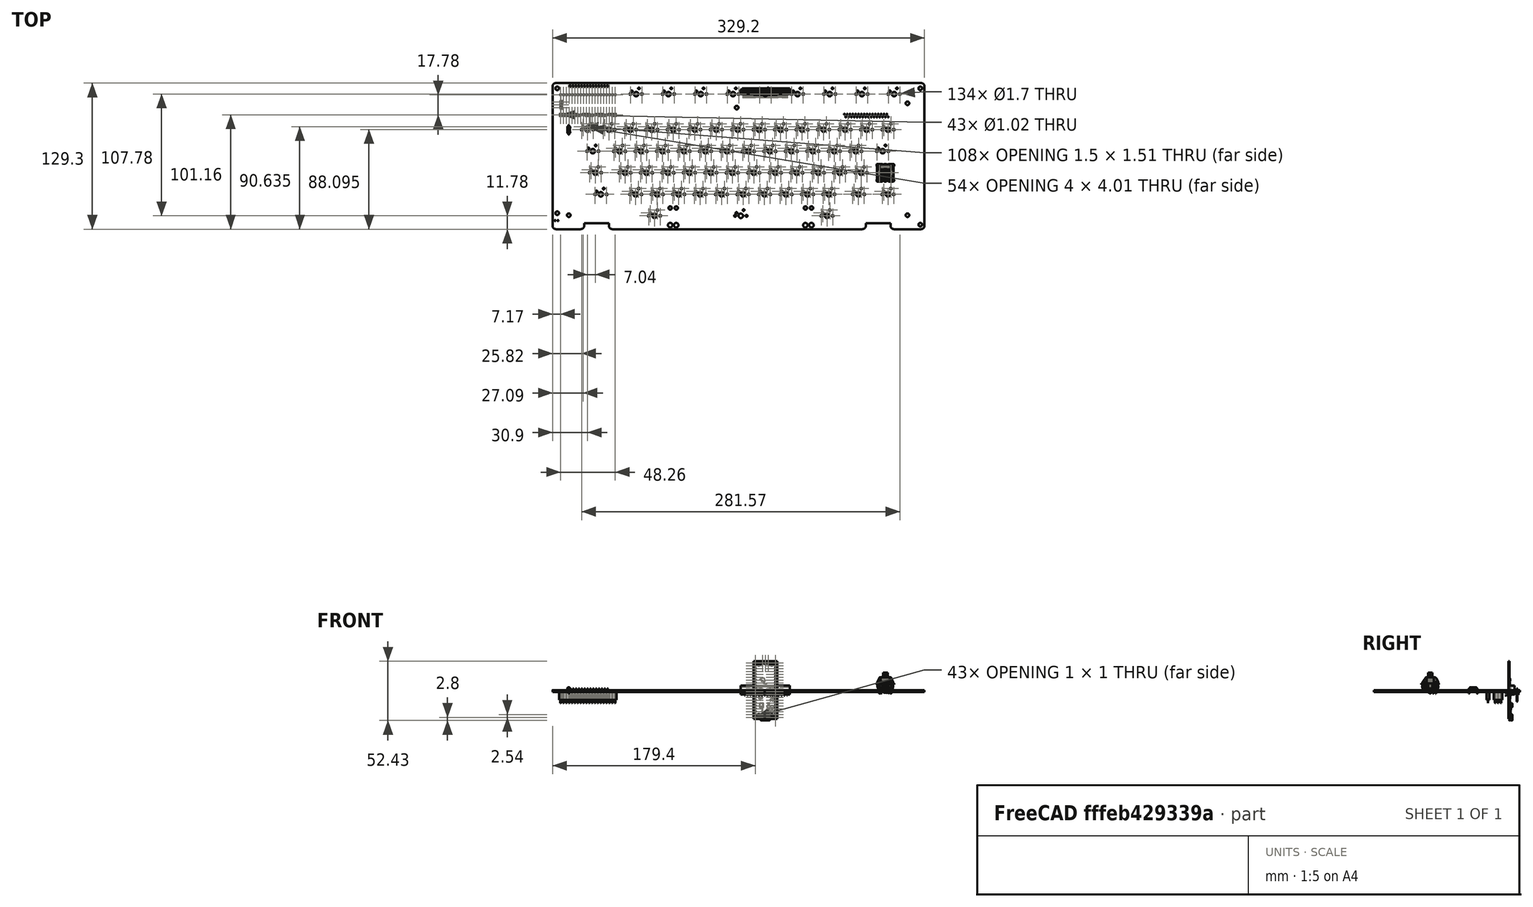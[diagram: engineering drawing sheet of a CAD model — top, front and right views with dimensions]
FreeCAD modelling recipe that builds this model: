
FCSTD DOCUMENT  (FreeCAD 0.19R)
Label: Atari130XE_MX
License: All rights reserved
LicenseURL: http://en.wikipedia.org/wiki/All_rights_reserved
objects: App::Link×126, Part::Feature×53, App::Part×7, PartDesign::CoordinateSystem×1, Sketcher::SketchObject×1
note: 55 computed .brp shape members not serialized (recipe doc carries the construction recipe); baked Part::Feature solids carry a one-line shape summary decoded from their .brp

FEATURE [PartDesign::CoordinateSystem] Local_CS_673a
  AttacherType = Attacher::AttachEngine3D
FEATURE [Part::Feature] Pcb_673a
  Placement = pos=(-211.16,32.61,0) rot=(0,0,1;0rad)
  shape: bbox 329.2 x 129.3 x 1.6 mm, 1031 faces (baked)
FEATURE [Sketcher::SketchObject] PCB_Sketch_673a
  FullyConstrained = false
  sketch-geometry (20):
    g0: LineSegment StartX=113.84 StartY=-119.55 StartZ=0 EndX=137.9 EndY=-119.55 EndZ=0
    g1: LineSegment StartX=88.94 StartY=-114.45 StartZ=0 EndX=88.94 EndY=-116.55 EndZ=0
    g2: LineSegment StartX=110.84 StartY=-114.45 StartZ=0 EndX=110.84 EndY=-116.55 EndZ=0
    g3: LineSegment StartX=88.94 StartY=-114.45 StartZ=0 EndX=110.84 EndY=-114.45 EndZ=0
    g4: LineSegment StartX=-135.4 StartY=-119.55 StartZ=0 EndX=85.94 EndY=-119.55 EndZ=0
    g5: LineSegment StartX=-138.4 StartY=-114.45 StartZ=0 EndX=-138.4 EndY=-116.55 EndZ=0
    g6: LineSegment StartX=-160.3 StartY=-114.45 StartZ=0 EndX=-138.4 EndY=-114.45 EndZ=0
    g7: LineSegment StartX=-160.3 StartY=-114.45 StartZ=0 EndX=-160.3 EndY=-116.55 EndZ=0
    g8: LineSegment StartX=-185.3 StartY=-119.55 StartZ=0 EndX=-163.3 EndY=-119.55 EndZ=0
    g9: LineSegment StartX=140.9 StartY=6.75 StartZ=0 EndX=140.9 EndY=-116.55 EndZ=0
    g10: LineSegment StartX=-185.3 StartY=9.75 StartZ=0 EndX=137.9 EndY=9.75 EndZ=0
    g11: LineSegment StartX=-188.3 StartY=6.75 StartZ=0 EndX=-188.3 EndY=-116.55 EndZ=0
    g12: ArcOfCircle CenterX=113.84 CenterY=-116.55 CenterZ=0 NormalX=0 NormalY=0 NormalZ=1 AngleXU=0 Radius=3 StartAngle=3.14159 EndAngle=4.71239
    g13: ArcOfCircle CenterX=85.94 CenterY=-116.55 CenterZ=0 NormalX=0 NormalY=0 NormalZ=1 AngleXU=0 Radius=3 StartAngle=4.71239 EndAngle=6.28319
    g14: ArcOfCircle CenterX=-135.4 CenterY=-116.55 CenterZ=0 NormalX=0 NormalY=0 NormalZ=1 AngleXU=0 Radius=3 StartAngle=3.14159 EndAngle=4.71239
    g15: ArcOfCircle CenterX=-163.3 CenterY=-116.55 CenterZ=0 NormalX=0 NormalY=0 NormalZ=1 AngleXU=0 Radius=3 StartAngle=4.71239 EndAngle=6.28319
    g16: ArcOfCircle CenterX=137.9 CenterY=-116.55 CenterZ=0 NormalX=0 NormalY=0 NormalZ=1 AngleXU=0 Radius=3 StartAngle=4.71239 EndAngle=6.28319
    g17: ArcOfCircle CenterX=137.9 CenterY=6.75 CenterZ=0 NormalX=0 NormalY=0 NormalZ=1 AngleXU=0 Radius=3 StartAngle=0 EndAngle=1.5708
    g18: ArcOfCircle CenterX=-185.3 CenterY=-116.55 CenterZ=0 NormalX=0 NormalY=0 NormalZ=1 AngleXU=0 Radius=3 StartAngle=3.14159 EndAngle=4.71239
    g19: ArcOfCircle CenterX=-185.3 CenterY=6.75 CenterZ=0 NormalX=0 NormalY=0 NormalZ=1 AngleXU=0 Radius=3 StartAngle=1.5708 EndAngle=3.14159
  constraints (20):
    c: Coincident(g18,g11)
    c: Coincident(g19,g11)
    c: Coincident(g18,g8)
    c: Coincident(g10,g19)
    c: Coincident(g8,g15)
    c: Coincident(g7,g15)
    c: Coincident(g6,g7)
    c: Coincident(g5,g14)
    c: Coincident(g5,g6)
    c: Coincident(g4,g14)
    c: Coincident(g13,g4)
    c: Coincident(g1,g13)
    c: Coincident(g3,g1)
    c: Coincident(g12,g2)
    c: Coincident(g2,g3)
    c: Coincident(g12,g0)
    c: Coincident(g16,g0)
    c: Coincident(g10,g17)
    c: Coincident(g9,g16)
    c: Coincident(g17,g9)
FEATURE [App::Part] Board_Geoms_673a
  Group = -> [Local_CS_673a,Pcb_673a,PCB_Sketch_673a]
  Origin = -> Origin
FEATURE [Part::Feature] Shape  label="SW49_SW_Cherry_MX_PCB_cp_608261B0"
  Placement = pos=(106.24,-69.62,0) rot=(0,0,1;0rad)
  shape: bbox 15.61 x 15.61 x 18.61 mm, 942 faces, 7 solids (baked)
FEATURE [App::Link] SW49_SW_Cherry_MX_PCB_cp_608261B0_ln_  label="SW49_SW_Cherry_MX_PCB_cp_608261B0[2]"
  LinkPlacement = pos=(106.24,-69.62,0) rot=(0,0,1;0rad)
  LinkedObject = -> Shape
  Placement = pos=(106.24,-69.62,0) rot=(0,0,1;0rad)
FEATURE [App::Link] SW49_SW_Cherry_MX_PCB_cp_608261B0_ln_001  label="SW19_SW_Cherry_MX_PCB_cp_6082D2A1"
  LinkPlacement = pos=(-157.4,-31.45,0) rot=(0,0,1;0rad)
  LinkedObject = -> Shape
  Placement = pos=(-157.4,-31.45,0) rot=(0,0,1;0rad)
FEATURE [App::Link] SW49_SW_Cherry_MX_PCB_cp_608261B0_ln_002  label="SW19_SW_Cherry_MX_PCB_cp_6082D2A1[2]"
  LinkPlacement = pos=(-157.4,-31.45,0) rot=(0,0,1;0rad)
  LinkedObject = -> Shape
  Placement = pos=(-157.4,-31.45,0) rot=(0,0,1;0rad)
FEATURE [App::Link] SW49_SW_Cherry_MX_PCB_cp_608261B0_ln_003  label="SW13_SW_Cherry_MX_PCB_cp_6082D337"
  LinkPlacement = pos=(-43.4,-31.45,0) rot=(0,0,1;0rad)
  LinkedObject = -> Shape
  Placement = pos=(-43.4,-31.45,0) rot=(0,0,1;0rad)
FEATURE [App::Link] SW49_SW_Cherry_MX_PCB_cp_608261B0_ln_004  label="SW13_SW_Cherry_MX_PCB_cp_6082D337[2]"
  LinkPlacement = pos=(-43.4,-31.45,0) rot=(0,0,1;0rad)
  LinkedObject = -> Shape
  Placement = pos=(-43.4,-31.45,0) rot=(0,0,1;0rad)
FEATURE [App::Link] SW49_SW_Cherry_MX_PCB_cp_608261B0_ln_005  label="SW64_SW_Cherry_MX_PCB_cp_60826667"
  LinkPlacement = pos=(-114.7,-88.72,0) rot=(0,0,1;0rad)
  LinkedObject = -> Shape
  Placement = pos=(-114.7,-88.72,0) rot=(0,0,1;0rad)
FEATURE [App::Link] SW49_SW_Cherry_MX_PCB_cp_608261B0_ln_006  label="SW64_SW_Cherry_MX_PCB_cp_60826667[2]"
  LinkPlacement = pos=(-114.7,-88.72,0) rot=(0,0,1;0rad)
  LinkedObject = -> Shape
  Placement = pos=(-114.7,-88.72,0) rot=(0,0,1;0rad)
FEATURE [App::Link] SW49_SW_Cherry_MX_PCB_cp_608261B0_ln_007  label="SW27_SW_Cherry_MX_PCB_cp_6082C6BD"
  LinkPlacement = pos=(-33.94,-50.55,0) rot=(0,0,1;0rad)
  LinkedObject = -> Shape
  Placement = pos=(-33.94,-50.55,0) rot=(0,0,1;0rad)
FEATURE [App::Link] SW49_SW_Cherry_MX_PCB_cp_608261B0_ln_008  label="SW27_SW_Cherry_MX_PCB_cp_6082C6BD[2]"
  LinkPlacement = pos=(-33.94,-50.55,0) rot=(0,0,1;0rad)
  LinkedObject = -> Shape
  Placement = pos=(-33.94,-50.55,0) rot=(0,0,1;0rad)
FEATURE [App::Link] SW49_SW_Cherry_MX_PCB_cp_608261B0_ln_009  label="SW63_SW_Cherry_MX_PCB_cp_60826633"
  LinkPlacement = pos=(-95.7,-88.72,0) rot=(0,0,1;0rad)
  LinkedObject = -> Shape
  Placement = pos=(-95.7,-88.72,0) rot=(0,0,1;0rad)
FEATURE [App::Link] SW49_SW_Cherry_MX_PCB_cp_608261B0_ln_010  label="SW63_SW_Cherry_MX_PCB_cp_60826633[2]"
  LinkPlacement = pos=(-95.7,-88.72,0) rot=(0,0,1;0rad)
  LinkedObject = -> Shape
  Placement = pos=(-95.7,-88.72,0) rot=(0,0,1;0rad)
FEATURE [App::Link] SW49_SW_Cherry_MX_PCB_cp_608261B0_ln_011  label="SW31_SW_Cherry_MX_PCB_cp_6082C672"
  LinkPlacement = pos=(-109.94,-50.55,0) rot=(0,0,1;0rad)
  LinkedObject = -> Shape
  Placement = pos=(-109.94,-50.55,0) rot=(0,0,1;0rad)
FEATURE [App::Link] SW49_SW_Cherry_MX_PCB_cp_608261B0_ln_012  label="SW31_SW_Cherry_MX_PCB_cp_6082C672[2]"
  LinkPlacement = pos=(-109.94,-50.55,0) rot=(0,0,1;0rad)
  LinkedObject = -> Shape
  Placement = pos=(-109.94,-50.55,0) rot=(0,0,1;0rad)
FEATURE [App::Link] SW49_SW_Cherry_MX_PCB_cp_608261B0_ln_013  label="SW61_SW_Cherry_MX_PCB_cp_608265FF"
  LinkPlacement = pos=(-57.7,-88.72,0) rot=(0,0,1;0rad)
  LinkedObject = -> Shape
  Placement = pos=(-57.7,-88.72,0) rot=(0,0,1;0rad)
FEATURE [App::Link] SW49_SW_Cherry_MX_PCB_cp_608261B0_ln_014  label="SW61_SW_Cherry_MX_PCB_cp_608265FF[2]"
  LinkPlacement = pos=(-57.7,-88.72,0) rot=(0,0,1;0rad)
  LinkedObject = -> Shape
  Placement = pos=(-57.7,-88.72,0) rot=(0,0,1;0rad)
FEATURE [App::Link] SW49_SW_Cherry_MX_PCB_cp_608261B0_ln_015  label="SW20_SW_Cherry_MX_PCB_cp_6082C753"
  LinkPlacement = pos=(-14.94,-50.55,0) rot=(0,0,1;0rad)
  LinkedObject = -> Shape
  Placement = pos=(-14.94,-50.55,0) rot=(0,0,1;0rad)
FEATURE [App::Link] SW49_SW_Cherry_MX_PCB_cp_608261B0_ln_016  label="SW20_SW_Cherry_MX_PCB_cp_6082C753[2]"
  LinkPlacement = pos=(-14.94,-50.55,0) rot=(0,0,1;0rad)
  LinkedObject = -> Shape
  Placement = pos=(-14.94,-50.55,0) rot=(0,0,1;0rad)
FEATURE [App::Link] SW49_SW_Cherry_MX_PCB_cp_608261B0_ln_017  label="SW28_SW_Cherry_MX_PCB_cp_6082C708"
  LinkPlacement = pos=(-52.94,-50.55,0) rot=(0,0,1;0rad)
  LinkedObject = -> Shape
  Placement = pos=(-52.94,-50.55,0) rot=(0,0,1;0rad)
FEATURE [App::Link] SW49_SW_Cherry_MX_PCB_cp_608261B0_ln_018  label="SW28_SW_Cherry_MX_PCB_cp_6082C708[2]"
  LinkPlacement = pos=(-52.94,-50.55,0) rot=(0,0,1;0rad)
  LinkedObject = -> Shape
  Placement = pos=(-52.94,-50.55,0) rot=(0,0,1;0rad)
FEATURE [App::Link] SW49_SW_Cherry_MX_PCB_cp_608261B0_ln_019  label="SW40_SW_Cherry_MX_PCB_cp_61426050"
  LinkPlacement = pos=(84.84,-69.62,0) rot=(0,0,1;0rad)
  LinkedObject = -> Shape
  Placement = pos=(84.84,-69.62,0) rot=(0,0,1;0rad)
FEATURE [App::Link] SW49_SW_Cherry_MX_PCB_cp_608261B0_ln_020  label="SW40_SW_Cherry_MX_PCB_cp_61426050[2]"
  LinkPlacement = pos=(84.84,-69.62,0) rot=(0,0,1;0rad)
  LinkedObject = -> Shape
  Placement = pos=(84.84,-69.62,0) rot=(0,0,1;0rad)
FEATURE [App::Link] SW49_SW_Cherry_MX_PCB_cp_608261B0_ln_021  label="SW56_SW_Cherry_MX_PCB_cp_6082654A"
  LinkPlacement = pos=(56.3,-88.72,0) rot=(0,0,1;0rad)
  LinkedObject = -> Shape
  Placement = pos=(56.3,-88.72,0) rot=(0,0,1;0rad)
FEATURE [App::Link] SW49_SW_Cherry_MX_PCB_cp_608261B0_ln_022  label="SW56_SW_Cherry_MX_PCB_cp_6082654A[2]"
  LinkPlacement = pos=(56.3,-88.72,0) rot=(0,0,1;0rad)
  LinkedObject = -> Shape
  Placement = pos=(56.3,-88.72,0) rot=(0,0,1;0rad)
FEATURE [App::Link] SW49_SW_Cherry_MX_PCB_cp_608261B0_ln_023  label="SW38_SW_Cherry_MX_PCB_cp_60826530"
  LinkPlacement = pos=(46.84,-69.62,0) rot=(0,0,1;0rad)
  LinkedObject = -> Shape
  Placement = pos=(46.84,-69.62,0) rot=(0,0,1;0rad)
FEATURE [App::Link] SW49_SW_Cherry_MX_PCB_cp_608261B0_ln_024  label="SW38_SW_Cherry_MX_PCB_cp_60826530[2]"
  LinkPlacement = pos=(46.84,-69.62,0) rot=(0,0,1;0rad)
  LinkedObject = -> Shape
  Placement = pos=(46.84,-69.62,0) rot=(0,0,1;0rad)
FEATURE [App::Link] SW49_SW_Cherry_MX_PCB_cp_608261B0_ln_025  label="SW47_SW_Cherry_MX_PCB_cp_608264FC"
  LinkPlacement = pos=(-105.16,-69.62,0) rot=(0,0,1;0rad)
  LinkedObject = -> Shape
  Placement = pos=(-105.16,-69.62,0) rot=(0,0,1;0rad)
FEATURE [App::Link] SW49_SW_Cherry_MX_PCB_cp_608261B0_ln_026  label="SW47_SW_Cherry_MX_PCB_cp_608264FC[2]"
  LinkPlacement = pos=(-105.16,-69.62,0) rot=(0,0,1;0rad)
  LinkedObject = -> Shape
  Placement = pos=(-105.16,-69.62,0) rot=(0,0,1;0rad)
FEATURE [App::Link] SW49_SW_Cherry_MX_PCB_cp_608261B0_ln_027  label="SW29_SW_Cherry_MX_PCB_cp_6082CC99"
  LinkPlacement = pos=(-71.94,-50.55,0) rot=(0,0,1;0rad)
  LinkedObject = -> Shape
  Placement = pos=(-71.94,-50.55,0) rot=(0,0,1;0rad)
FEATURE [App::Link] SW49_SW_Cherry_MX_PCB_cp_608261B0_ln_028  label="SW29_SW_Cherry_MX_PCB_cp_6082CC99[2]"
  LinkPlacement = pos=(-71.94,-50.55,0) rot=(0,0,1;0rad)
  LinkedObject = -> Shape
  Placement = pos=(-71.94,-50.55,0) rot=(0,0,1;0rad)
FEATURE [App::Link] SW49_SW_Cherry_MX_PCB_cp_608261B0_ln_029  label="SW32_SW_Cherry_MX_PCB_cp_6082C87F"
  LinkPlacement = pos=(-128.94,-50.55,0) rot=(0,0,1;0rad)
  LinkedObject = -> Shape
  Placement = pos=(-128.94,-50.55,0) rot=(0,0,1;0rad)
FEATURE [App::Link] SW49_SW_Cherry_MX_PCB_cp_608261B0_ln_030  label="SW32_SW_Cherry_MX_PCB_cp_6082C87F[2]"
  LinkPlacement = pos=(-128.94,-50.55,0) rot=(0,0,1;0rad)
  LinkedObject = -> Shape
  Placement = pos=(-128.94,-50.55,0) rot=(0,0,1;0rad)
FEATURE [App::Link] SW49_SW_Cherry_MX_PCB_cp_608261B0_ln_031  label="SW39_SW_Cherry_MX_PCB_cp_6082645C"
  LinkPlacement = pos=(65.84,-69.62,0) rot=(0,0,1;0rad)
  LinkedObject = -> Shape
  Placement = pos=(65.84,-69.62,0) rot=(0,0,1;0rad)
FEATURE [App::Link] SW49_SW_Cherry_MX_PCB_cp_608261B0_ln_032  label="SW39_SW_Cherry_MX_PCB_cp_6082645C[2]"
  LinkPlacement = pos=(65.84,-69.62,0) rot=(0,0,1;0rad)
  LinkedObject = -> Shape
  Placement = pos=(65.84,-69.62,0) rot=(0,0,1;0rad)
FEATURE [App::Link] SW49_SW_Cherry_MX_PCB_cp_608261B0_ln_033  label="SW55_SW_Cherry_MX_PCB_cp_60826442"
  LinkPlacement = pos=(37.3,-88.72,0) rot=(0,0,1;0rad)
  LinkedObject = -> Shape
  Placement = pos=(37.3,-88.72,0) rot=(0,0,1;0rad)
FEATURE [App::Link] SW49_SW_Cherry_MX_PCB_cp_608261B0_ln_034  label="SW55_SW_Cherry_MX_PCB_cp_60826442[2]"
  LinkPlacement = pos=(37.3,-88.72,0) rot=(0,0,1;0rad)
  LinkedObject = -> Shape
  Placement = pos=(37.3,-88.72,0) rot=(0,0,1;0rad)
FEATURE [App::Link] SW49_SW_Cherry_MX_PCB_cp_608261B0_ln_035  label="SW23_SW_Cherry_MX_PCB_cp_6082C834"
  LinkPlacement = pos=(42.06,-50.55,0) rot=(0,0,1;0rad)
  LinkedObject = -> Shape
  Placement = pos=(42.06,-50.55,0) rot=(0,0,1;0rad)
FEATURE [App::Link] SW49_SW_Cherry_MX_PCB_cp_608261B0_ln_036  label="SW23_SW_Cherry_MX_PCB_cp_6082C834[2]"
  LinkPlacement = pos=(42.06,-50.55,0) rot=(0,0,1;0rad)
  LinkedObject = -> Shape
  Placement = pos=(42.06,-50.55,0) rot=(0,0,1;0rad)
FEATURE [App::Link] SW49_SW_Cherry_MX_PCB_cp_608261B0_ln_037  label="SW22_SW_Cherry_MX_PCB_cp_6082CDC5"
  LinkPlacement = pos=(23.06,-50.55,0) rot=(0,0,1;0rad)
  LinkedObject = -> Shape
  Placement = pos=(23.06,-50.55,0) rot=(0,0,1;0rad)
FEATURE [App::Link] SW49_SW_Cherry_MX_PCB_cp_608261B0_ln_038  label="SW22_SW_Cherry_MX_PCB_cp_6082CDC5[2]"
  LinkPlacement = pos=(23.06,-50.55,0) rot=(0,0,1;0rad)
  LinkedObject = -> Shape
  Placement = pos=(23.06,-50.55,0) rot=(0,0,1;0rad)
FEATURE [App::Link] SW49_SW_Cherry_MX_PCB_cp_608261B0_ln_039  label="SW51_SW_Cherry_MX_PCB_cp_608263DA"
  LinkPlacement = pos=(-19.7,-88.72,0) rot=(0,0,1;0rad)
  LinkedObject = -> Shape
  Placement = pos=(-19.7,-88.72,0) rot=(0,0,1;0rad)
FEATURE [App::Link] SW49_SW_Cherry_MX_PCB_cp_608261B0_ln_040  label="SW51_SW_Cherry_MX_PCB_cp_608263DA[2]"
  LinkPlacement = pos=(-19.7,-88.72,0) rot=(0,0,1;0rad)
  LinkedObject = -> Shape
  Placement = pos=(-19.7,-88.72,0) rot=(0,0,1;0rad)
FEATURE [App::Link] SW49_SW_Cherry_MX_PCB_cp_608261B0_ln_041  label="SW53_SW_Cherry_MX_PCB_cp_608263C0"
  LinkPlacement = pos=(-0.7,-88.72,0) rot=(0,0,1;0rad)
  LinkedObject = -> Shape
  Placement = pos=(-0.7,-88.72,0) rot=(0,0,1;0rad)
FEATURE [App::Link] SW49_SW_Cherry_MX_PCB_cp_608261B0_ln_042  label="SW53_SW_Cherry_MX_PCB_cp_608263C0[2]"
  LinkPlacement = pos=(-0.7,-88.72,0) rot=(0,0,1;0rad)
  LinkedObject = -> Shape
  Placement = pos=(-0.7,-88.72,0) rot=(0,0,1;0rad)
FEATURE [App::Link] SW49_SW_Cherry_MX_PCB_cp_608261B0_ln_043  label="SW5_SW_Cherry_MX_PCB_cp_6082D5DA"
  LinkPlacement = pos=(51.6,-31.45,0) rot=(0,0,1;0rad)
  LinkedObject = -> Shape
  Placement = pos=(51.6,-31.45,0) rot=(0,0,1;0rad)
FEATURE [App::Link] SW49_SW_Cherry_MX_PCB_cp_608261B0_ln_044  label="SW5_SW_Cherry_MX_PCB_cp_6082D5DA[2]"
  LinkPlacement = pos=(51.6,-31.45,0) rot=(0,0,1;0rad)
  LinkedObject = -> Shape
  Placement = pos=(51.6,-31.45,0) rot=(0,0,1;0rad)
FEATURE [App::Link] SW49_SW_Cherry_MX_PCB_cp_608261B0_ln_045  label="SW37_SW_Cherry_MX_PCB_cp_6082636E"
  LinkPlacement = pos=(27.84,-69.62,0) rot=(0,0,1;0rad)
  LinkedObject = -> Shape
  Placement = pos=(27.84,-69.62,0) rot=(0,0,1;0rad)
FEATURE [App::Link] SW49_SW_Cherry_MX_PCB_cp_608261B0_ln_046  label="SW37_SW_Cherry_MX_PCB_cp_6082636E[2]"
  LinkPlacement = pos=(27.84,-69.62,0) rot=(0,0,1;0rad)
  LinkedObject = -> Shape
  Placement = pos=(27.84,-69.62,0) rot=(0,0,1;0rad)
FEATURE [App::Link] SW49_SW_Cherry_MX_PCB_cp_608261B0_ln_047  label="SW36_SW_Cherry_MX_PCB_cp_60826354"
  LinkPlacement = pos=(8.84,-69.62,0) rot=(0,0,1;0rad)
  LinkedObject = -> Shape
  Placement = pos=(8.84,-69.62,0) rot=(0,0,1;0rad)
FEATURE [App::Link] SW49_SW_Cherry_MX_PCB_cp_608261B0_ln_048  label="SW36_SW_Cherry_MX_PCB_cp_60826354[2]"
  LinkPlacement = pos=(8.84,-69.62,0) rot=(0,0,1;0rad)
  LinkedObject = -> Shape
  Placement = pos=(8.84,-69.62,0) rot=(0,0,1;0rad)
FEATURE [App::Link] SW49_SW_Cherry_MX_PCB_cp_608261B0_ln_049  label="SW35_SW_Cherry_MX_PCB_cp_6082633A"
  LinkPlacement = pos=(-10.16,-69.62,0) rot=(0,0,1;0rad)
  LinkedObject = -> Shape
  Placement = pos=(-10.16,-69.62,0) rot=(0,0,1;0rad)
FEATURE [App::Link] SW49_SW_Cherry_MX_PCB_cp_608261B0_ln_050  label="SW35_SW_Cherry_MX_PCB_cp_6082633A[2]"
  LinkPlacement = pos=(-10.16,-69.62,0) rot=(0,0,1;0rad)
  LinkedObject = -> Shape
  Placement = pos=(-10.16,-69.62,0) rot=(0,0,1;0rad)
FEATURE [App::Link] SW49_SW_Cherry_MX_PCB_cp_608261B0_ln_051  label="SW57_SW_Cherry_MX_PCB_cp_60826320"
  LinkPlacement = pos=(108.6,-88.72,0) rot=(0,0,1;0rad)
  LinkedObject = -> Shape
  Placement = pos=(108.6,-88.72,0) rot=(0,0,1;0rad)
FEATURE [App::Link] SW49_SW_Cherry_MX_PCB_cp_608261B0_ln_052  label="SW57_SW_Cherry_MX_PCB_cp_60826320[2]"
  LinkPlacement = pos=(108.6,-88.72,0) rot=(0,0,1;0rad)
  LinkedObject = -> Shape
  Placement = pos=(108.6,-88.72,0) rot=(0,0,1;0rad)
FEATURE [App::Link] SW49_SW_Cherry_MX_PCB_cp_608261B0_ln_053  label="SW21_SW_Cherry_MX_PCB_cp_6082C915"
  LinkPlacement = pos=(4.06,-50.55,0) rot=(0,0,1;0rad)
  LinkedObject = -> Shape
  Placement = pos=(4.06,-50.55,0) rot=(0,0,1;0rad)
FEATURE [App::Link] SW49_SW_Cherry_MX_PCB_cp_608261B0_ln_054  label="SW21_SW_Cherry_MX_PCB_cp_6082C915[2]"
  LinkPlacement = pos=(4.06,-50.55,0) rot=(0,0,1;0rad)
  LinkedObject = -> Shape
  Placement = pos=(4.06,-50.55,0) rot=(0,0,1;0rad)
FEATURE [App::Link] SW49_SW_Cherry_MX_PCB_cp_608261B0_ln_055  label="SW43_SW_Cherry_MX_PCB_cp_608262D2"
  LinkPlacement = pos=(-29.16,-69.62,0) rot=(0,0,1;0rad)
  LinkedObject = -> Shape
  Placement = pos=(-29.16,-69.62,0) rot=(0,0,1;0rad)
FEATURE [App::Link] SW49_SW_Cherry_MX_PCB_cp_608261B0_ln_056  label="SW43_SW_Cherry_MX_PCB_cp_608262D2[2]"
  LinkPlacement = pos=(-29.16,-69.62,0) rot=(0,0,1;0rad)
  LinkedObject = -> Shape
  Placement = pos=(-29.16,-69.62,0) rot=(0,0,1;0rad)
FEATURE [App::Link] SW49_SW_Cherry_MX_PCB_cp_608261B0_ln_057  label="SW6_SW_Cherry_MX_PCB_cp_6082D4F9"
  LinkPlacement = pos=(70.6,-31.45,0) rot=(0,0,1;0rad)
  LinkedObject = -> Shape
  Placement = pos=(70.6,-31.45,0) rot=(0,0,1;0rad)
FEATURE [App::Link] SW49_SW_Cherry_MX_PCB_cp_608261B0_ln_058  label="SW6_SW_Cherry_MX_PCB_cp_6082D4F9[2]"
  LinkPlacement = pos=(70.6,-31.45,0) rot=(0,0,1;0rad)
  LinkedObject = -> Shape
  Placement = pos=(70.6,-31.45,0) rot=(0,0,1;0rad)
FEATURE [App::Link] SW49_SW_Cherry_MX_PCB_cp_608261B0_ln_059  label="SW44_SW_Cherry_MX_PCB_cp_6082629E"
  LinkPlacement = pos=(-48.16,-69.62,0) rot=(0,0,1;0rad)
  LinkedObject = -> Shape
  Placement = pos=(-48.16,-69.62,0) rot=(0,0,1;0rad)
FEATURE [App::Link] SW49_SW_Cherry_MX_PCB_cp_608261B0_ln_060  label="SW44_SW_Cherry_MX_PCB_cp_6082629E[2]"
  LinkPlacement = pos=(-48.16,-69.62,0) rot=(0,0,1;0rad)
  LinkedObject = -> Shape
  Placement = pos=(-48.16,-69.62,0) rot=(0,0,1;0rad)
FEATURE [App::Link] SW49_SW_Cherry_MX_PCB_cp_608261B0_ln_061  label="SW25_SW_Cherry_MX_PCB_cp_6082C9AB"
  LinkPlacement = pos=(80.06,-50.55,0) rot=(0,0,1;0rad)
  LinkedObject = -> Shape
  Placement = pos=(80.06,-50.55,0) rot=(0,0,1;0rad)
FEATURE [App::Link] SW49_SW_Cherry_MX_PCB_cp_608261B0_ln_062  label="SW25_SW_Cherry_MX_PCB_cp_6082C9AB[2]"
  LinkPlacement = pos=(80.06,-50.55,0) rot=(0,0,1;0rad)
  LinkedObject = -> Shape
  Placement = pos=(80.06,-50.55,0) rot=(0,0,1;0rad)
FEATURE [App::Link] SW49_SW_Cherry_MX_PCB_cp_608261B0_ln_063  label="SW30_SW_Cherry_MX_PCB_cp_6082CCE4"
  LinkPlacement = pos=(-90.94,-50.55,0) rot=(0,0,1;0rad)
  LinkedObject = -> Shape
  Placement = pos=(-90.94,-50.55,0) rot=(0,0,1;0rad)
FEATURE [App::Link] SW49_SW_Cherry_MX_PCB_cp_608261B0_ln_064  label="SW30_SW_Cherry_MX_PCB_cp_6082CCE4[2]"
  LinkPlacement = pos=(-90.94,-50.55,0) rot=(0,0,1;0rad)
  LinkedObject = -> Shape
  Placement = pos=(-90.94,-50.55,0) rot=(0,0,1;0rad)
FEATURE [App::Link] SW49_SW_Cherry_MX_PCB_cp_608261B0_ln_065  label="SW7_SW_Cherry_MX_PCB_cp_6082D463"
  LinkPlacement = pos=(89.6,-31.45,0) rot=(0,0,1;0rad)
  LinkedObject = -> Shape
  Placement = pos=(89.6,-31.45,0) rot=(0,0,1;0rad)
FEATURE [App::Link] SW49_SW_Cherry_MX_PCB_cp_608261B0_ln_066  label="SW7_SW_Cherry_MX_PCB_cp_6082D463[2]"
  LinkPlacement = pos=(89.6,-31.45,0) rot=(0,0,1;0rad)
  LinkedObject = -> Shape
  Placement = pos=(89.6,-31.45,0) rot=(0,0,1;0rad)
FEATURE [App::Link] SW49_SW_Cherry_MX_PCB_cp_608261B0_ln_067  label="SW24_SW_Cherry_MX_PCB_cp_6082CA41"
  LinkPlacement = pos=(61.06,-50.55,0) rot=(0,0,1;0rad)
  LinkedObject = -> Shape
  Placement = pos=(61.06,-50.55,0) rot=(0,0,1;0rad)
FEATURE [App::Link] SW49_SW_Cherry_MX_PCB_cp_608261B0_ln_068  label="SW24_SW_Cherry_MX_PCB_cp_6082CA41[2]"
  LinkPlacement = pos=(61.06,-50.55,0) rot=(0,0,1;0rad)
  LinkedObject = -> Shape
  Placement = pos=(61.06,-50.55,0) rot=(0,0,1;0rad)
FEATURE [App::Link] SW49_SW_Cherry_MX_PCB_cp_608261B0_ln_069  label="SW46_SW_Cherry_MX_PCB_cp_6100000000.0"
  LinkPlacement = pos=(-86.16,-69.62,0) rot=(0,0,1;0rad)
  LinkedObject = -> Shape
  Placement = pos=(-86.16,-69.62,0) rot=(0,0,1;0rad)
FEATURE [App::Link] SW49_SW_Cherry_MX_PCB_cp_608261B0_ln_070  label="SW46_SW_Cherry_MX_PCB_cp_6100000000.0[2]"
  LinkPlacement = pos=(-86.16,-69.62,0) rot=(0,0,1;0rad)
  LinkedObject = -> Shape
  Placement = pos=(-86.16,-69.62,0) rot=(0,0,1;0rad)
FEATURE [App::Link] SW49_SW_Cherry_MX_PCB_cp_608261B0_ln_071  label="SW54_SW_Cherry_MX_PCB_cp_60826196"
  LinkPlacement = pos=(18.3,-88.72,0) rot=(0,0,1;0rad)
  LinkedObject = -> Shape
  Placement = pos=(18.3,-88.72,0) rot=(0,0,1;0rad)
FEATURE [App::Link] SW49_SW_Cherry_MX_PCB_cp_608261B0_ln_072  label="SW54_SW_Cherry_MX_PCB_cp_60826196[2]"
  LinkPlacement = pos=(18.3,-88.72,0) rot=(0,0,1;0rad)
  LinkedObject = -> Shape
  Placement = pos=(18.3,-88.72,0) rot=(0,0,1;0rad)
FEATURE [App::Link] SW49_SW_Cherry_MX_PCB_cp_608261B0_ln_073  label="SW62_SW_Cherry_MX_PCB_cp_6082617C"
  LinkPlacement = pos=(-76.7,-88.72,0) rot=(0,0,1;0rad)
  LinkedObject = -> Shape
  Placement = pos=(-76.7,-88.72,0) rot=(0,0,1;0rad)
FEATURE [App::Link] SW49_SW_Cherry_MX_PCB_cp_608261B0_ln_074  label="SW62_SW_Cherry_MX_PCB_cp_6082617C[2]"
  LinkPlacement = pos=(-76.7,-88.72,0) rot=(0,0,1;0rad)
  LinkedObject = -> Shape
  Placement = pos=(-76.7,-88.72,0) rot=(0,0,1;0rad)
FEATURE [App::Link] SW49_SW_Cherry_MX_PCB_cp_608261B0_ln_075  label="SW8_SW_Cherry_MX_PCB_cp_6082D625"
  LinkPlacement = pos=(108.6,-31.45,0) rot=(0,0,1;0rad)
  LinkedObject = -> Shape
  Placement = pos=(108.6,-31.45,0) rot=(0,0,1;0rad)
FEATURE [App::Link] SW49_SW_Cherry_MX_PCB_cp_608261B0_ln_076  label="SW8_SW_Cherry_MX_PCB_cp_6082D625[2]"
  LinkPlacement = pos=(108.6,-31.45,0) rot=(0,0,1;0rad)
  LinkedObject = -> Shape
  Placement = pos=(108.6,-31.45,0) rot=(0,0,1;0rad)
FEATURE [App::Link] SW49_SW_Cherry_MX_PCB_cp_608261B0_ln_077  label="SW60_SW_Cherry_MX_PCB_cp_60826148"
  LinkPlacement = pos=(-38.7,-88.72,0) rot=(0,0,1;0rad)
  LinkedObject = -> Shape
  Placement = pos=(-38.7,-88.72,0) rot=(0,0,1;0rad)
FEATURE [App::Link] SW49_SW_Cherry_MX_PCB_cp_608261B0_ln_078  label="SW60_SW_Cherry_MX_PCB_cp_60826148[2]"
  LinkPlacement = pos=(-38.7,-88.72,0) rot=(0,0,1;0rad)
  LinkedObject = -> Shape
  Placement = pos=(-38.7,-88.72,0) rot=(0,0,1;0rad)
FEATURE [App::Link] SW49_SW_Cherry_MX_PCB_cp_608261B0_ln_079  label="SW48_SW_Cherry_MX_PCB_cp_6082612E"
  LinkPlacement = pos=(-124.16,-69.62,0) rot=(0,0,1;0rad)
  LinkedObject = -> Shape
  Placement = pos=(-124.16,-69.62,0) rot=(0,0,1;0rad)
FEATURE [App::Link] SW49_SW_Cherry_MX_PCB_cp_608261B0_ln_080  label="SW48_SW_Cherry_MX_PCB_cp_6082612E[2]"
  LinkPlacement = pos=(-124.16,-69.62,0) rot=(0,0,1;0rad)
  LinkedObject = -> Shape
  Placement = pos=(-124.16,-69.62,0) rot=(0,0,1;0rad)
FEATURE [App::Link] SW49_SW_Cherry_MX_PCB_cp_608261B0_ln_081  label="SW3_SW_Cherry_MX_PCB_cp_6082D382"
  LinkPlacement = pos=(13.6,-31.45,0) rot=(0,0,1;0rad)
  LinkedObject = -> Shape
  Placement = pos=(13.6,-31.45,0) rot=(0,0,1;0rad)
FEATURE [App::Link] SW49_SW_Cherry_MX_PCB_cp_608261B0_ln_082  label="SW3_SW_Cherry_MX_PCB_cp_6082D382[2]"
  LinkPlacement = pos=(13.6,-31.45,0) rot=(0,0,1;0rad)
  LinkedObject = -> Shape
  Placement = pos=(13.6,-31.45,0) rot=(0,0,1;0rad)
FEATURE [App::Link] SW49_SW_Cherry_MX_PCB_cp_608261B0_ln_083  label="SW2_SW_Cherry_MX_PCB_cp_6082D2EC"
  LinkPlacement = pos=(-5.4,-31.45,0) rot=(0,0,1;0rad)
  LinkedObject = -> Shape
  Placement = pos=(-5.4,-31.45,0) rot=(0,0,1;0rad)
FEATURE [App::Link] SW49_SW_Cherry_MX_PCB_cp_608261B0_ln_084  label="SW2_SW_Cherry_MX_PCB_cp_6082D2EC[2]"
  LinkPlacement = pos=(-5.4,-31.45,0) rot=(0,0,1;0rad)
  LinkedObject = -> Shape
  Placement = pos=(-5.4,-31.45,0) rot=(0,0,1;0rad)
FEATURE [App::Link] SW49_SW_Cherry_MX_PCB_cp_608261B0_ln_085  label="SW1_SW_Cherry_MX_PCB_cp_6082D6BB"
  LinkPlacement = pos=(-24.4,-31.45,0) rot=(0,0,1;0rad)
  LinkedObject = -> Shape
  Placement = pos=(-24.4,-31.45,0) rot=(0,0,1;0rad)
FEATURE [App::Link] SW49_SW_Cherry_MX_PCB_cp_608261B0_ln_086  label="SW1_SW_Cherry_MX_PCB_cp_6082D6BB[2]"
  LinkPlacement = pos=(-24.4,-31.45,0) rot=(0,0,1;0rad)
  LinkedObject = -> Shape
  Placement = pos=(-24.4,-31.45,0) rot=(0,0,1;0rad)
FEATURE [App::Link] SW49_SW_Cherry_MX_PCB_cp_608261B0_ln_087  label="SW14_SW_Cherry_MX_PCB_cp_6082D418"
  LinkPlacement = pos=(-62.4,-31.45,0) rot=(0,0,1;0rad)
  LinkedObject = -> Shape
  Placement = pos=(-62.4,-31.45,0) rot=(0,0,1;0rad)
FEATURE [App::Link] SW49_SW_Cherry_MX_PCB_cp_608261B0_ln_088  label="SW14_SW_Cherry_MX_PCB_cp_6082D418[2]"
  LinkPlacement = pos=(-62.4,-31.45,0) rot=(0,0,1;0rad)
  LinkedObject = -> Shape
  Placement = pos=(-62.4,-31.45,0) rot=(0,0,1;0rad)
FEATURE [App::Link] SW49_SW_Cherry_MX_PCB_cp_608261B0_ln_089  label="SW15_SW_Cherry_MX_PCB_cp_6082D544"
  LinkPlacement = pos=(-81.4,-31.45,0) rot=(0,0,1;0rad)
  LinkedObject = -> Shape
  Placement = pos=(-81.4,-31.45,0) rot=(0,0,1;0rad)
FEATURE [App::Link] SW49_SW_Cherry_MX_PCB_cp_608261B0_ln_090  label="SW15_SW_Cherry_MX_PCB_cp_6082D544[2]"
  LinkPlacement = pos=(-81.4,-31.45,0) rot=(0,0,1;0rad)
  LinkedObject = -> Shape
  Placement = pos=(-81.4,-31.45,0) rot=(0,0,1;0rad)
FEATURE [App::Link] SW49_SW_Cherry_MX_PCB_cp_608261B0_ln_091  label="SW16_SW_Cherry_MX_PCB_cp_6082D4AE"
  LinkPlacement = pos=(-100.4,-31.45,0) rot=(0,0,1;0rad)
  LinkedObject = -> Shape
  Placement = pos=(-100.4,-31.45,0) rot=(0,0,1;0rad)
FEATURE [App::Link] SW49_SW_Cherry_MX_PCB_cp_608261B0_ln_092  label="SW16_SW_Cherry_MX_PCB_cp_6082D4AE[2]"
  LinkPlacement = pos=(-100.4,-31.45,0) rot=(0,0,1;0rad)
  LinkedObject = -> Shape
  Placement = pos=(-100.4,-31.45,0) rot=(0,0,1;0rad)
FEATURE [App::Link] SW49_SW_Cherry_MX_PCB_cp_608261B0_ln_093  label="SW17_SW_Cherry_MX_PCB_cp_6082D670"
  LinkPlacement = pos=(-119.4,-31.45,0) rot=(0,0,1;0rad)
  LinkedObject = -> Shape
  Placement = pos=(-119.4,-31.45,0) rot=(0,0,1;0rad)
FEATURE [App::Link] SW49_SW_Cherry_MX_PCB_cp_608261B0_ln_094  label="SW17_SW_Cherry_MX_PCB_cp_6082D670[2]"
  LinkPlacement = pos=(-119.4,-31.45,0) rot=(0,0,1;0rad)
  LinkedObject = -> Shape
  Placement = pos=(-119.4,-31.45,0) rot=(0,0,1;0rad)
FEATURE [App::Link] SW49_SW_Cherry_MX_PCB_cp_608261B0_ln_095  label="SW18_SW_Cherry_MX_PCB_cp_6082D58F"
  LinkPlacement = pos=(-138.4,-31.45,0) rot=(0,0,1;0rad)
  LinkedObject = -> Shape
  Placement = pos=(-138.4,-31.45,0) rot=(0,0,1;0rad)
FEATURE [App::Link] SW49_SW_Cherry_MX_PCB_cp_608261B0_ln_096  label="SW18_SW_Cherry_MX_PCB_cp_6082D58F[2]"
  LinkPlacement = pos=(-138.4,-31.45,0) rot=(0,0,1;0rad)
  LinkedObject = -> Shape
  Placement = pos=(-138.4,-31.45,0) rot=(0,0,1;0rad)
FEATURE [App::Link] SW49_SW_Cherry_MX_PCB_cp_608261B0_ln_097  label="SW4_SW_Cherry_MX_PCB_cp_6082D3CD"
  LinkPlacement = pos=(32.6,-31.45,0) rot=(0,0,1;0rad)
  LinkedObject = -> Shape
  Placement = pos=(32.6,-31.45,0) rot=(0,0,1;0rad)
FEATURE [App::Link] SW49_SW_Cherry_MX_PCB_cp_608261B0_ln_098  label="SW4_SW_Cherry_MX_PCB_cp_6082D3CD[2]"
  LinkPlacement = pos=(32.6,-31.45,0) rot=(0,0,1;0rad)
  LinkedObject = -> Shape
  Placement = pos=(32.6,-31.45,0) rot=(0,0,1;0rad)
FEATURE [App::Link] SW49_SW_Cherry_MX_PCB_cp_608261B0_ln_099  label="SW45_SW_Cherry_MX_PCB_cp_61BDBE23"
  LinkPlacement = pos=(-67.16,-69.62,0) rot=(0,0,1;0rad)
  LinkedObject = -> Shape
  Placement = pos=(-67.16,-69.62,0) rot=(0,0,1;0rad)
FEATURE [App::Link] SW49_SW_Cherry_MX_PCB_cp_608261B0_ln_100  label="SW45_SW_Cherry_MX_PCB_cp_61BDBE23[2]"
  LinkPlacement = pos=(-67.16,-69.62,0) rot=(0,0,1;0rad)
  LinkedObject = -> Shape
  Placement = pos=(-67.16,-69.62,0) rot=(0,0,1;0rad)
FEATURE [Part::Feature] Part__Feature  label="SOLID"
  shape: bbox 43.4 x 8.502 x 9.002 mm, 897 faces (baked)
FEATURE [Part::Feature] Part__Feature001  label="COMPOUND"
  shape: bbox 40.7 x 7.3 x 9.3 mm, 0 faces, 0 solids (baked)
FEATURE [App::Part] _20443245  label="J2_520443245_61BBBDC0"
  Group = -> [Part__Feature,Part__Feature001]
  Origin = -> Origin008
  Placement = pos=(89.5,-15.4,-1.6) rot=(-1,0,0;1.5708rad)
FEATURE [App::Link] SW49_SW_Cherry_MX_PCB_cp_608261B0_ln_101  label="SW67_SW_Cherry_MX_PCB_cp_6082638C"
  LinkPlacement = pos=(-145.55,-88.72,0) rot=(0,0,1;0rad)
  LinkedObject = -> Shape
  Placement = pos=(-145.55,-88.72,0) rot=(0,0,1;0rad)
FEATURE [App::Link] SW49_SW_Cherry_MX_PCB_cp_608261B0_ln_102  label="SW67_SW_Cherry_MX_PCB_cp_6082638C[2]"
  LinkPlacement = pos=(-145.55,-88.72,0) rot=(0,0,1;0rad)
  LinkedObject = -> Shape
  Placement = pos=(-145.55,-88.72,0) rot=(0,0,1;0rad)
FEATURE [App::Link] SW49_SW_Cherry_MX_PCB_cp_608261B0_ln_103  label="SW65_SW_Cherry_MX_PCB_cp_6164DBC0"
  LinkPlacement = pos=(-28.575,0,0) rot=(0,0,1;0rad)
  LinkedObject = -> Shape
  Placement = pos=(-28.575,0,0) rot=(0,0,1;0rad)
FEATURE [App::Link] SW49_SW_Cherry_MX_PCB_cp_608261B0_ln_104  label="SW58_SW_Cherry_MX_PCB_cp_6164DBA8"
  LinkPlacement = pos=(-57.15,0,0) rot=(0,0,1;0rad)
  LinkedObject = -> Shape
  Placement = pos=(-57.15,0,0) rot=(0,0,1;0rad)
FEATURE [App::Link] SW49_SW_Cherry_MX_PCB_cp_608261B0_ln_105  label="SW41_SW_Cherry_MX_PCB_cp_6164DB90"
  LinkPlacement = pos=(-85.725,0,0) rot=(0,0,1;0rad)
  LinkedObject = -> Shape
  Placement = pos=(-85.725,0,0) rot=(0,0,1;0rad)
FEATURE [App::Link] SW49_SW_Cherry_MX_PCB_cp_608261B0_ln_106  label="SW34_SW_Cherry_MX_PCB_cp_6164DB78"
  LinkPlacement = pos=(-114.3,0,0) rot=(0,0,1;0rad)
  LinkedObject = -> Shape
  Placement = pos=(-114.3,0,0) rot=(0,0,1;0rad)
FEATURE [Part::Feature] Shape001  label="R1_R_Axial_DIN0207_L63mm_D25mm_P762mm_Horizontal_6148158F"
  Placement = pos=(-173.94,-35.435,0) rot=(0,0,1;1.5708rad)
  shape: bbox 2.706 x 8.418 x 5.603 mm, 15 faces (baked)
FEATURE [Part::Feature] Shape002  label="J1_PinHeader_1x14_P254mm_Vertical_61481338"
  Placement = pos=(-172.72,7.11,-1.6) rot=(-0.707107,0.707107,0;3.14159rad)
  shape: bbox 35.56 x 2.54 x 11.54 mm, 340 faces (baked)
FEATURE [App::Link] SW49_SW_Cherry_MX_PCB_cp_608261B0_ln_107  label="SW66_SW_Cherry_MX_PCB_cp_60826400.0"
  LinkPlacement = pos=(82.425,-88.72,0) rot=(0,0,1;0rad)
  LinkedObject = -> Shape
  Placement = pos=(82.425,-88.72,0) rot=(0,0,1;0rad)
FEATURE [App::Link] SW49_SW_Cherry_MX_PCB_cp_608261B0_ln_108  label="SW66_SW_Cherry_MX_PCB_cp_60826400.0[2]"
  LinkPlacement = pos=(82.425,-88.72,0) rot=(0,0,1;0rad)
  LinkedObject = -> Shape
  Placement = pos=(82.425,-88.72,0) rot=(0,0,1;0rad)
FEATURE [App::Link] SW49_SW_Cherry_MX_PCB_cp_608261B0_ln_109  label="SW42_SW_Cherry_MX_PCB_cp_608261CE"
  LinkPlacement = pos=(-150.36,-69.62,0) rot=(0,0,1;0rad)
  LinkedObject = -> Shape
  Placement = pos=(-150.36,-69.62,0) rot=(0,0,1;0rad)
FEATURE [App::Link] SW49_SW_Cherry_MX_PCB_cp_608261B0_ln_110  label="SW42_SW_Cherry_MX_PCB_cp_608261CE[2]"
  LinkPlacement = pos=(-150.36,-69.62,0) rot=(0,0,1;0rad)
  LinkedObject = -> Shape
  Placement = pos=(-150.36,-69.62,0) rot=(0,0,1;0rad)
FEATURE [App::Link] SW49_SW_Cherry_MX_PCB_cp_608261B0_ln_111  label="SW9_SW_Cherry_MX_PCB_cp_60826597"
  LinkPlacement = pos=(28.5,0,0) rot=(0,0,1;0rad)
  LinkedObject = -> Shape
  Placement = pos=(28.5,0,0) rot=(0,0,1;0rad)
FEATURE [App::Link] SW49_SW_Cherry_MX_PCB_cp_608261B0_ln_112  label="SW10_SW_Cherry_MX_PCB_cp_60826516"
  LinkPlacement = pos=(57,0,0) rot=(0,0,1;0rad)
  LinkedObject = -> Shape
  Placement = pos=(57,0,0) rot=(0,0,1;0rad)
FEATURE [App::Link] SW49_SW_Cherry_MX_PCB_cp_608261B0_ln_113  label="SW12_SW_Cherry_MX_PCB_cp_608264AA"
  LinkPlacement = pos=(114,0,0) rot=(0,0,1;0rad)
  LinkedObject = -> Shape
  Placement = pos=(114,0,0) rot=(0,0,1;0rad)
FEATURE [App::Link] SW49_SW_Cherry_MX_PCB_cp_608261B0_ln_114  label="SW11_SW_Cherry_MX_PCB_cp_6082640E"
  LinkPlacement = pos=(85.5,0,0) rot=(0,0,1;0rad)
  LinkedObject = -> Shape
  Placement = pos=(85.5,0,0) rot=(0,0,1;0rad)
FEATURE [App::Link] SW49_SW_Cherry_MX_PCB_cp_608261B0_ln_115  label="SW59_SW_Cherry_MX_PCB_cp_608262EC"
  LinkedObject = -> Shape
FEATURE [Part::Feature] Shape003  label="D1_LED_D3.0mm_Horizontal_O1.27mm_Z2.0mm_6081B78C"
  Placement = pos=(-186,-112,0) rot=(0,0,1;0rad)
  shape: bbox 3.47 x 6.87 x 5.9 mm, 33 faces (baked)
FEATURE [App::Link] SW49_SW_Cherry_MX_PCB_cp_608261B0_ln_116  label="SW33_SW_Cherry_MX_PCB_cp_6087B499"
  LinkPlacement = pos=(-152.64,-50.55,0) rot=(0,0,1;0rad)
  LinkedObject = -> Shape
  Placement = pos=(-152.64,-50.55,0) rot=(0,0,1;0rad)
FEATURE [App::Link] SW49_SW_Cherry_MX_PCB_cp_608261B0_ln_117  label="SW33_SW_Cherry_MX_PCB_cp_6087B499[2]"
  LinkPlacement = pos=(-152.64,-50.55,0) rot=(0,0,1;0rad)
  LinkedObject = -> Shape
  Placement = pos=(-152.64,-50.55,0) rot=(0,0,1;0rad)
FEATURE [App::Link] SW49_SW_Cherry_MX_PCB_cp_608261B0_ln_118  label="SW26_SW_Cherry_MX_PCB_cp_6082C7E9"
  LinkPlacement = pos=(103.86,-50.55,0) rot=(0,0,1;0rad)
  LinkedObject = -> Shape
  Placement = pos=(103.86,-50.55,0) rot=(0,0,1;0rad)
FEATURE [App::Link] SW49_SW_Cherry_MX_PCB_cp_608261B0_ln_119  label="SW26_SW_Cherry_MX_PCB_cp_6082C7E9[2]"
  LinkPlacement = pos=(103.86,-50.55,0) rot=(0,0,1;0rad)
  LinkedObject = -> Shape
  Placement = pos=(103.86,-50.55,0) rot=(0,0,1;0rad)
FEATURE [App::Link] SW49_SW_Cherry_MX_PCB_cp_608261B0_ln_120  label="SW52_SW_Cherry_MX_PCB_cp_61E0FACB[2]"
  LinkPlacement = pos=(-21.67,-107.77,0) rot=(0,0,1;0rad)
  LinkedObject = -> Shape
  Placement = pos=(-21.67,-107.77,0) rot=(0,0,1;0rad)
FEATURE [App::Link] SW49_SW_Cherry_MX_PCB_cp_608261B0_ln_121  label="SW68_SW_Cherry_MX_PCB_cp_61E0E50F"
  LinkPlacement = pos=(-98,-107.73,0) rot=(0,0,1;0rad)
  LinkedObject = -> Shape
  Placement = pos=(-98,-107.73,0) rot=(0,0,1;0rad)
FEATURE [App::Link] SW49_SW_Cherry_MX_PCB_cp_608261B0_ln_122  label="SW68_SW_Cherry_MX_PCB_cp_61E0E50F[2]"
  LinkPlacement = pos=(-98,-107.73,0) rot=(0,0,1;0rad)
  LinkedObject = -> Shape
  Placement = pos=(-98,-107.73,0) rot=(0,0,1;0rad)
FEATURE [App::Link] SW49_SW_Cherry_MX_PCB_cp_608261B0_ln_123  label="SW69_SW_Cherry_MX_PCB_cp_61E0E539"
  LinkPlacement = pos=(54.6,-107.76,0) rot=(0,0,1;0rad)
  LinkedObject = -> Shape
  Placement = pos=(54.6,-107.76,0) rot=(0,0,1;0rad)
FEATURE [App::Link] SW49_SW_Cherry_MX_PCB_cp_608261B0_ln_124  label="SW69_SW_Cherry_MX_PCB_cp_61E0E539[2]"
  LinkPlacement = pos=(54.6,-107.76,0) rot=(0,0,1;0rad)
  LinkedObject = -> Shape
  Placement = pos=(54.6,-107.76,0) rot=(0,0,1;0rad)
FEATURE [App::Part] Top_673a
  Group = -> [Shape,SW49_SW_Cherry_MX_PCB_cp_608261B0_ln_,SW49_SW_Cherry_MX_PCB_cp_608261B0_ln_001,SW49_SW_Cherry_MX_PCB_cp_608261B0_ln_002,SW49_SW_Cherry_MX_PCB_cp_608261B0_ln_003,SW49_SW_Cherry_MX_PCB_cp_608261B0_ln_004,SW49_SW_Cherry_MX_PCB_cp_608261B0_ln_005,SW49_SW_Cherry_MX_PCB_cp_608261B0_ln_006,SW49_SW_Cherry_MX_PCB_cp_608261B0_ln_007,SW49_SW_Cherry_MX_PCB_cp_608261B0_ln_008,+118 more]
  Origin = -> Origin003
FEATURE [Part::Feature] Part__Feature002  label="PCB, Raspberry Pi Pico-R3"
  shape: bbox 21 x 1 x 51 mm, 416 faces (baked)
FEATURE [Part::Feature] Part__Feature003  label="MicroUSB Port, Raspberry Pi Pico-R3"
  Placement = pos=(0,0.5,-24.35) rot=(0,1,0;3.14159rad)
  shape: bbox 8 x 2.95 x 5.462 mm, 1230 faces, 7 solids (baked)
FEATURE [Part::Feature] Part__Feature004  label="RP2040 Microcontroller, Raspberry Pi Pico-R3"
  Placement = pos=(0,0.5,0.5) rot=(0,0,1;0rad)
  shape: bbox 7 x 0.9 x 7 mm, 6 faces (baked)
FEATURE [Part::Feature] Part__Feature005  label="SW1, Tact Switch, Raspberry Pi Pico-R3"
  Placement = pos=(-3.5,0.5,-13.5) rot=(0,0,1;0rad)
  shape: bbox 3.2 x 2.5 x 4.25 mm, 17 faces (baked)
FEATURE [Part::Feature] Part__Feature006  label="D1, Diode, Schottky, Raspberry Pi Pico-R3"
  Placement = pos=(6,0.5,-19) rot=(0,0,1;0rad)
  shape: bbox 1.65 x 0.95 x 3.6 mm, 14 faces (baked)
FEATURE [Part::Feature] Part__Feature007  label="D2, QSME-C194, LED, Raspberry Pi Pico-R3"
  Placement = pos=(-5.8,0.5,-20.8) rot=(0,0,1;0rad)
  shape: bbox 1.6 x 0.55 x 0.8 mm, 6 faces (baked)
FEATURE [Part::Feature] Part__Feature008  label="L1, Inductor, Raspberry Pi Pico-R3"
  Placement = pos=(6,0.5,-14.6) rot=(0,0,1;0rad)
  shape: bbox 2 x 1.2 x 2.5 mm, 6 faces (baked)
FEATURE [Part::Feature] Part__Feature009  label="U2, RT6150B-33GQW, Buck Boost Converter, Raspberry Pi Pico-R3"
  Placement = pos=(3,0.5,-14.6) rot=(0,0,1;0rad)
  shape: bbox 2.5 x 0.8 x 2.5 mm, 6 faces (baked)
FEATURE [Part::Feature] Part__Feature010  label="U3, W25Q16JVUXIQ, Serial NOR Flash 16 Mbit, Raspberry Pi Pico-R3"
  Placement = pos=(-3.8,0.5,-6.4) rot=(0,0,1;0rad)
  shape: bbox 2 x 0.8 x 3 mm, 6 faces (baked)
FEATURE [Part::Feature] Part__Feature011  label="Q1, MOSFET, DMG1012T, Raspberry Pi Pico-R3"
  Placement = pos=(6.5,0.5,-7.2) rot=(0,0,1;0rad)
  shape: bbox 1.6 x 0.6 x 1.8 mm, 18 faces (baked)
FEATURE [Part::Feature] Part__Feature012  label="X1, X12M000000S096, 12 Mhz Crystal Resonator, Raspberry Pi Pico-R3"
  Placement = pos=(-2.2,0.5,9) rot=(0,0,1;0rad)
  shape: bbox 3.2 x 0.6 x 2.5 mm, 18 faces (baked)
FEATURE [Part::Feature] Part__Feature013  label="SMD Resistor, Configurable, Raspberry Pi Pico-R3_R1"
  Placement = pos=(6.2,0.5,1) rot=(0,1,0;1.5708rad)
  shape: bbox 1 x 0.35 x 0.5 mm, 18 faces, 3 solids (baked)
FEATURE [Part::Feature] Part__Feature014  label="SMD Resistor, Configurable, Raspberry Pi Pico-R3_R2"
  Placement = pos=(3.5,0.5,-18.6) rot=(0,1,0;1.5708rad)
  shape: bbox 1 x 0.35 x 0.5 mm, 18 faces, 3 solids (baked)
FEATURE [Part::Feature] Part__Feature015  label="SMD Resistor, Configurable, Raspberry Pi Pico-R3_R3"
  Placement = pos=(-2.7,0.5,-17.8) rot=(0,1,0;1.5708rad)
  shape: bbox 1 x 0.35 x 0.5 mm, 18 faces, 3 solids (baked)
FEATURE [Part::Feature] Part__Feature016  label="SMD Resistor, Configurable, Raspberry Pi Pico-R3_R4"
  Placement = pos=(-5.5,0.5,-5.4) rot=(0,1,0;3.14159rad)
  shape: bbox 0.5 x 0.35 x 1 mm, 18 faces, 3 solids (baked)
FEATURE [Part::Feature] Part__Feature017  label="SMD Resistor, Configurable, Raspberry Pi Pico-R3_R5"
  Placement = pos=(7,0.5,-9.6) rot=(0,1,0;3.14159rad)
  shape: bbox 0.5 x 0.35 x 1 mm, 18 faces, 3 solids (baked)
FEATURE [Part::Feature] Part__Feature018  label="SMD Resistor, Configurable, Raspberry Pi Pico-R3_R6"
  Placement = pos=(6.5,0.5,-4.6) rot=(0,1,0;3.14159rad)
  shape: bbox 0.5 x 0.35 x 1 mm, 18 faces, 3 solids (baked)
FEATURE [Part::Feature] Part__Feature019  label="SMD Resistor, Configurable, Raspberry Pi Pico-R3_R7"
  Placement = pos=(4.5,0.5,-9) rot=(0,1,0;3.14159rad)
  shape: bbox 0.8 x 0.45 x 1.6 mm, 18 faces, 3 solids (baked)
FEATURE [Part::Feature] Part__Feature020  label="SMD Resistor, Configurable, Raspberry Pi Pico-R3_R8"
  Placement = pos=(-2.7,0.5,-18.8) rot=(0,1,0;1.5708rad)
  shape: bbox 1 x 0.35 x 0.5 mm, 18 faces, 3 solids (baked)
FEATURE [Part::Feature] Part__Feature021  label="SMD Resistor, Configurable, Raspberry Pi Pico-R3_R9"
  Placement = pos=(5.5,0.5,-4.6) rot=(0,1,0;3.14159rad)
  shape: bbox 0.5 x 0.35 x 1 mm, 18 faces, 3 solids (baked)
FEATURE [Part::Feature] Part__Feature022  label="SMD Resistor, Configurable, Raspberry Pi Pico-R3_R10"
  Placement = pos=(6.2,0.5,-1e-16) rot=(0,1,0;1.5708rad)
  shape: bbox 1 x 0.35 x 0.5 mm, 18 faces, 3 solids (baked)
FEATURE [Part::Feature] Part__Feature023  label="SMD Resistor, Configurable, Raspberry Pi Pico-R3_R11"
  Placement = pos=(-5.5,0.5,-7.4) rot=(0,0,1;0rad)
  shape: bbox 0.5 x 0.35 x 1 mm, 18 faces, 3 solids (baked)
FEATURE [Part::Feature] Part__Feature024  label="SMD Resistor, Configurable, Raspberry Pi Pico-R3_R12"
  Placement = pos=(0.8,0.5,-4.6) rot=(0,1,0;3.14159rad)
  shape: bbox 0.3 x 0.23 x 0.6 mm, 18 faces, 3 solids (baked)
FEATURE [Part::Feature] Part__Feature025  label="SMD Resistor, Configurable, Raspberry Pi Pico-R3_R13"
  Placement = pos=(1.4,0.5,-4.6) rot=(0,1,0;3.14159rad)
  shape: bbox 0.3 x 0.23 x 0.6 mm, 18 faces, 3 solids (baked)
FEATURE [Part::Feature] Part__Feature026  label="SMD Resistor, Configurable, Raspberry Pi Pico-R3_R14"
  Placement = pos=(-1.1,0.5,7) rot=(0,1,0;1.5708rad)
  shape: bbox 1 x 0.35 x 0.5 mm, 18 faces, 3 solids (baked)
FEATURE [Part::Feature] Part__Feature027  label="SMD Resistor, Configurable, Raspberry Pi Pico-R3_R15"
  Placement = pos=(-1.7,0.5,6.2) rot=(0,1,0;1.5708rad)
  shape: bbox 1 x 0.35 x 0.5 mm, 18 faces, 3 solids (baked)
FEATURE [Part::Feature] Part__Feature028  label="SMD Capacitor, Configurable, Raspberry Pi Pico-R3_C1"
  Placement = pos=(3,0.5,-17) rot=(0,1,0;1.5708rad)
  shape: bbox 2 x 1.25 x 1.25 mm, 18 faces, 3 solids (baked)
FEATURE [Part::Feature] Part__Feature029  label="SMD Capacitor, Configurable, Raspberry Pi Pico-R3_C2"
  Placement = pos=(3,0.5,-12) rot=(0,1,0;1.5708rad)
  shape: bbox 2 x 1.25 x 1.25 mm, 18 faces, 3 solids (baked)
FEATURE [Part::Feature] Part__Feature030  label="SMD Capacitor, Configurable, Raspberry Pi Pico-R3_C3"
  Placement = pos=(6,0.5,-9.4) rot=(0,0,1;0rad)
  shape: bbox 0.3 x 0.3 x 0.6 mm, 18 faces, 3 solids (baked)
FEATURE [Part::Feature] Part__Feature031  label="SMD Capacitor, Configurable, Raspberry Pi Pico-R3_C4"
  Placement = pos=(-4.5,0.5,-2.1) rot=(0,-1,0;1.5708rad)
  shape: bbox 0.6 x 0.3 x 0.3 mm, 18 faces, 3 solids (baked)
FEATURE [Part::Feature] Part__Feature032  label="SMD Capacitor, Configurable, Raspberry Pi Pico-R3_C5"
  Placement = pos=(-4.5,0.5,1.5) rot=(0,-1,0;1.5708rad)
  shape: bbox 0.6 x 0.3 x 0.3 mm, 18 faces, 3 solids (baked)
FEATURE [Part::Feature] Part__Feature033  label="SMD Capacitor, Configurable, Raspberry Pi Pico-R3_C6"
  Placement = pos=(4.6,0.5,1.9) rot=(0,1,0;0.785398rad)
  shape: bbox 0.6364 x 0.3 x 0.6364 mm, 18 faces, 3 solids (baked)
FEATURE [Part::Feature] Part__Feature034  label="SMD Capacitor, Configurable, Raspberry Pi Pico-R3_C7"
  Placement = pos=(4.5,0.5,-2.4) rot=(0,-1,0;1.5708rad)
  shape: bbox 0.6 x 0.3 x 0.3 mm, 18 faces, 3 solids (baked)
FEATURE [Part::Feature] Part__Feature035  label="SMD Capacitor, Configurable, Raspberry Pi Pico-R3_C8"
  Placement = pos=(0,0.5,5.5) rot=(0,0,1;0rad)
  shape: bbox 0.3 x 0.3 x 0.6 mm, 18 faces, 3 solids (baked)
FEATURE [Part::Feature] Part__Feature036  label="SMD Capacitor, Configurable, Raspberry Pi Pico-R3_C9"
  Placement = pos=(0.8,0.5,5.5) rot=(0,0,1;0rad)
  shape: bbox 0.3 x 0.3 x 0.6 mm, 18 faces, 3 solids (baked)
FEATURE [Part::Feature] Part__Feature037  label="SMD Capacitor, Configurable, Raspberry Pi Pico-R3_C10"
  Placement = pos=(0,0.5,-4.6) rot=(0,0,1;0rad)
  shape: bbox 0.3 x 0.3 x 0.6 mm, 18 faces, 3 solids (baked)
FEATURE [Part::Feature] Part__Feature038  label="SMD Capacitor, Configurable, Raspberry Pi Pico-R3_C11"
  Placement = pos=(-0.7,0.5,-4.6) rot=(0,0,1;0rad)
  shape: bbox 0.3 x 0.3 x 0.6 mm, 18 faces, 3 solids (baked)
FEATURE [Part::Feature] Part__Feature039  label="SMD Capacitor, Configurable, Raspberry Pi Pico-R3_C12"
  Placement = pos=(2.2,0.5,-4.6) rot=(0,0,1;0rad)
  shape: bbox 0.5 x 0.5 x 1 mm, 18 faces, 3 solids (baked)
FEATURE [Part::Feature] Part__Feature040  label="SMD Capacitor, Configurable, Raspberry Pi Pico-R3_C13"
  Placement = pos=(4.6,0.5,-4.6) rot=(0,0,1;0rad)
  shape: bbox 0.5 x 0.5 x 1 mm, 18 faces, 3 solids (baked)
FEATURE [Part::Feature] Part__Feature041  label="SMD Capacitor, Configurable, Raspberry Pi Pico-R3_C14"
  Placement = pos=(3.2,0.5,-4.6) rot=(0,0,1;0rad)
  shape: bbox 0.5 x 0.5 x 1 mm, 18 faces, 3 solids (baked)
FEATURE [Part::Feature] Part__Feature042  label="SMD Capacitor, Configurable, Raspberry Pi Pico-R3_C15"
  Placement = pos=(-4.5,0.5,-8.8) rot=(0,0,1;0rad)
  shape: bbox 0.3 x 0.3 x 0.6 mm, 18 faces, 3 solids (baked)
FEATURE [Part::Feature] Part__Feature043  label="SMD Capacitor, Configurable, Raspberry Pi Pico-R3_C16"
  Placement = pos=(-4.6,0.5,9.6) rot=(0,0,1;0rad)
  shape: bbox 0.3 x 0.3 x 0.6 mm, 18 faces, 3 solids (baked)
FEATURE [Part::Feature] Part__Feature044  label="SMD Capacitor, Configurable, Raspberry Pi Pico-R3_C17"
  Placement = pos=(0,0.5,8.5) rot=(0,0,1;0rad)
  shape: bbox 0.3 x 0.3 x 0.6 mm, 18 faces, 3 solids (baked)
FEATURE [Part::Feature] Part__Feature045  label="SMD Capacitor, Configurable, Raspberry Pi Pico-R3_C18"
  Placement = pos=(-4.7,0.5,-3.1) rot=(0,-1,0;1.5708rad)
  shape: bbox 1 x 0.5 x 0.5 mm, 18 faces, 3 solids (baked)
FEATURE [App::Part] Raspberry_Pi_Pico_R3  label="U1_Raspberry Pi Pico-R3_61FD71E1"
  Group = -> [Part__Feature002,Part__Feature003,Part__Feature004,Part__Feature005,Part__Feature006,Part__Feature007,Part__Feature008,Part__Feature009,Part__Feature010,Part__Feature011,Part__Feature012,Part__Feature013,Part__Feature014,Part__Feature015,Part__Feature016,Part__Feature017,Part__Feature018,Part__Feature019,Part__Feature020,Part__Feature021,Part__Feature022,Part__Feature023,Part__Feature024,+21 more]
  Origin = -> Origin009
  Placement = pos=(-157,-9.5,-9.1) rot=(0.57735,0.57735,-0.57735;4.18879rad)
FEATURE [Part::Feature] Shape004  label="U1_PinSocket_1x20_P254mm_Vertical_61FD71E1[2]"
  Placement = pos=(-133,-18.5,-8.6) rot=(0,0,-1;1.5708rad)
  shape: bbox 50.8 x 2.54 x 10.1 mm, 630 faces (baked)
FEATURE [App::Link] U1_PinSocket_1x20_P254mm_Vertical_61FD71E1_2__ln_  label="U1_PinSocket_1x20_P254mm_Vertical_61FD71E1[3]"
  LinkPlacement = pos=(-133,-0.5,-8.6) rot=(0,0,-1;1.5708rad)
  LinkedObject = -> Shape004
  Placement = pos=(-133,-0.5,-8.6) rot=(0,0,-1;1.5708rad)
FEATURE [Part::Feature] Shape005  label="U1_PinSocket_1x03_P254mm_Vertical_61FD71E1[4]"
  Placement = pos=(-180.5,-12,-8.6) rot=(0,0,1;3.14159rad)
  shape: bbox 2.54 x 7.62 x 10.1 mm, 103 faces (baked)
FEATURE [App::Part] Bot_673a
  Group = -> [_20443245,Shape002,Raspberry_Pi_Pico_R3,Shape004,U1_PinSocket_1x20_P254mm_Vertical_61FD71E1_2__ln_,Shape005]
  Origin = -> Origin004
FEATURE [App::Part] Step_Models_673a
  Group = -> [Top_673a,Bot_673a]
  Origin = -> Origin002
FEATURE [App::Part] Board_673a  label="Atari130MX"
  Group = -> [Board_Geoms_673a,Step_Models_673a]
  Origin = -> Origin001
